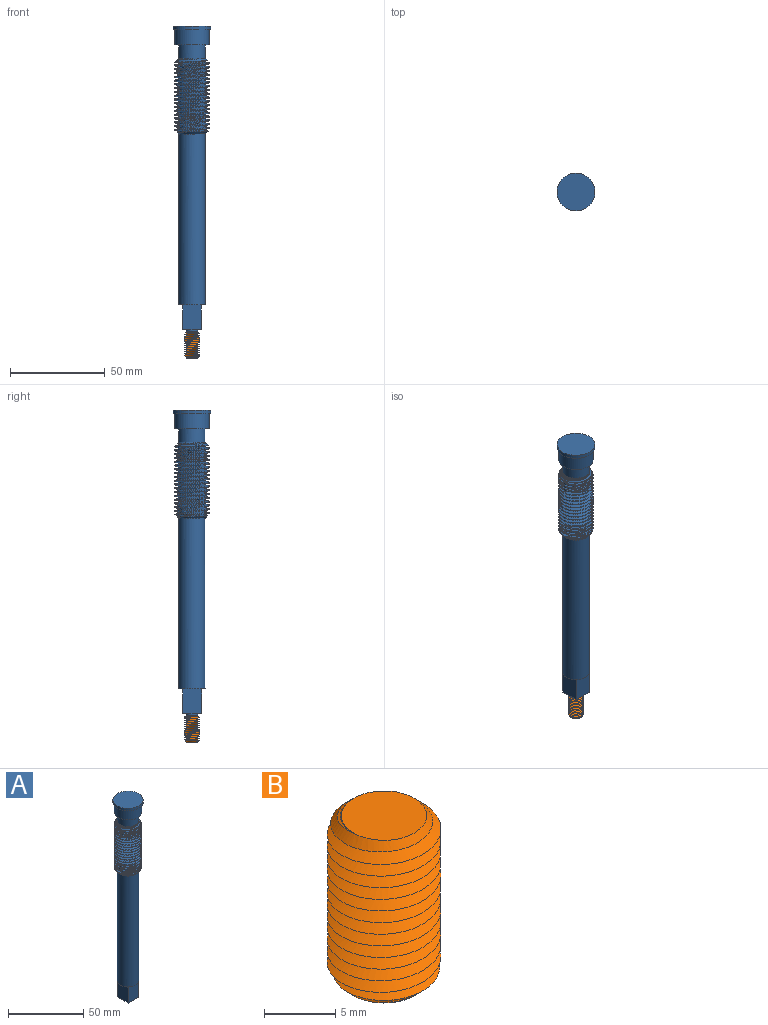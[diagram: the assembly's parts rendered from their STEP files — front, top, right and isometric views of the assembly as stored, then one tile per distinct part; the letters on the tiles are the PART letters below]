
ASSEMBLY  parts=2 mates=1
PART A: 39 faces, bbox 20x20.8x161 mm
  f0: plane 14x14mm, normal (0,0,-1), area 57.3mm2, adj f26,f27,f28,f29,f30
  f1: cylinder r=10mm len=20mm, axis (0,0,1), area 125.7mm2, adj f2,f3
  f2: plane 20x20mm, normal (0,0,-1), area 59.7mm2, adj f1,f4
  f3: plane 20x20mm, normal (0,0,1), area 314.2mm2, adj f1
  f4: cylinder r=9mm len=18mm, axis (0,0,1), area 452.4mm2, adj f2,f5
  f5: plane 18x18mm, normal (0,0,-1), area 100.5mm2, adj f4,f6
  f6: cylinder r=7mm len=14mm, axis (0,0,1), area 321.6mm2, adj f5,f7,f34,f35,f38
  f7: cylinder r=7mm len=14mm, axis (0,0,1), area 22mm2, adj f6,f8,f34,f35
  f8: cylinder r=7mm len=14mm, axis (0,0,1), area 22mm2, adj f7,f9,f34,f35
  f9: cylinder r=7mm len=14mm, axis (0,0,1), area 22mm2, adj f8,f10,f34,f35
  f10: cylinder r=7mm len=14mm, axis (0,0,1), area 22mm2, adj f9,f11,f34,f35
  f11: cylinder r=7mm len=14mm, axis (0,0,1), area 22mm2, adj f10,f12,f34,f35
  f12: cylinder r=7mm len=14mm, axis (0,0,1), area 22mm2, adj f11,f13,f34,f35
  f13: cylinder r=7mm len=14mm, axis (0,0,1), area 22mm2, adj f12,f14,f34,f35
  f14: cylinder r=7mm len=14mm, axis (0,0,1), area 22mm2, adj f13,f15,f34,f35
  f15: cylinder r=7mm len=14mm, axis (0,0,1), area 22mm2, adj f14,f16,f34,f35
  f16: cylinder r=7mm len=14mm, axis (0,0,1), area 22mm2, adj f15,f17,f34,f35
  f17: cylinder r=7mm len=14mm, axis (0,0,1), area 22mm2, adj f16,f18,f34,f35
  f18: cylinder r=7mm len=14mm, axis (0,0,1), area 22mm2, adj f17,f19,f34,f35
  f19: cylinder r=7mm len=14mm, axis (0,0,1), area 22mm2, adj f18,f20,f34,f35
  f20: cylinder r=7mm len=14mm, axis (0,0,1), area 22mm2, adj f19,f21,f34,f35
  f21: cylinder r=7mm len=14mm, axis (0,0,1), area 22mm2, adj f20,f22,f34,f35
  f22: cylinder r=7mm len=14mm, axis (0,0,1), area 22mm2, adj f21,f23,f34,f35
  f23: cylinder r=7mm len=14mm, axis (0,0,1), area 22mm2, adj f22,f24,f34,f35
  f24: cylinder r=7mm len=14mm, axis (0,0,1), area 22mm2, adj f23,f25,f34,f35
  f25: cylinder r=7mm len=14mm, axis (0,0,1), area 22mm2, adj f24,f26,f34,f35
  f26: cylinder r=7mm len=91mm, axis (0,0,1), area 3966.7mm2, adj f0,f25,f34,f35,f37
  f27: plane 13x10mm, normal (-1,0,0), area 130mm2, adj f0,f28,f30,f31
  f28: plane 13x9.66mm, normal (0,1,0), area 125.6mm2, adj f0,f27,f29,f31
  f29: plane 13x10mm, normal (1,0,0), area 130mm2, adj f0,f28,f30,f31
  f30: plane 13x9.66mm, normal (0,-1,0), area 125.6mm2, adj f0,f27,f29,f31
  f31: plane 10x9.66mm, normal (0,0,-1), area 68.3mm2, adj f27,f28,f29,f30,f32
  f32: cylinder r=3mm len=6mm, axis (0,0,1), area 18.8mm2, adj f31,f33
  f33: plane 6x6mm, normal (0,0,-1), area 28.3mm2, adj f32
  f34: bspline ~40.83x20.78mm, area 1966.2mm2, adj f6,f7,f8,f9,f10,f11,f12,f13
  f35: bspline ~40.83x20.78mm, area 1967.4mm2, adj f6,f7,f8,f9,f10,f11,f12,f13
  f36: cylinder r=9mm len=36mm, axis (0,0,-1), area 296.5mm2, adj f34,f35,f37,f38
  f37: cone r=9mm half-angle=45deg, axis (0,0,1), area 69.6mm2, adj f26,f34,f35,f36
  f38: cone r=9mm half-angle=45deg, axis (0,0,-1), area 69.5mm2, adj f6,f34,f35,f36
PART B: 7 faces, bbox 8x9.2x15 mm
  f0: cylinder r=3mm len=14mm, axis (0,0,-1), area -3.6mm2, adj f1,f2,f4,f6
  f1: bspline ~14.66x9.24mm, area 318.8mm2, adj f0,f2,f3,f5
  f2: bspline ~14.66x9.24mm, area 320.1mm2, adj f0,f1,f3,f5
  f3: cone r=3mm half-angle=45deg, axis (0,0,1), area 14.7mm2, adj f1,f2,f4
  f4: plane 6x6mm, normal (0,0,-1), area 28.3mm2, adj f0,f3
  f5: cone r=3mm half-angle=45deg, axis (0,0,-1), area 14.7mm2, adj f1,f2,f6
  f6: plane 6x6mm, normal (0,0,1), area 28.3mm2, adj f0,f5
PLACE A t=(48.25,40.87,278.01)mm
PLACE B t=(48.25,40.87,100.01)mm
MATE fastened B.f5 <-> A.f32  axis (0,0,1) through (48.25,40.87,117.01)mm
